# Revit family: bfs-40_210ssua2_stua2_60Hz
name_source: partatom
category: 機械設備
units: mm (PartAtom-declared; Revit-internal decimal feet)

## family parameters
OmniClass タイトル = Centrifugal Fans
OmniClass 番号 = 23.75.35.17.27
パーツ タイプ = 割り込み
ロード時にボイドで切り取り = いいえ
丸型コネクタ寸法 = 直径を使用
作業面ベース = いいえ
共有 = いいえ
常に垂直 = はい
部屋計算ポイント = はい

## types (7) — shared parameters
Clearance Left = 450  [stored 1.47638 ft]
IfcExportAs = IfcFanType
IfcExportType = CENTRIFUGALFORWARDCURVED
MID静圧 = 0.0 Pa
MID風量 = 0.0 m³/h
OmniClassCode = 23-33 31 19 13 15
URL = https://www.mitsubishielectric.co.jp
Uniclass2015Code = Pr_65_67_29_12
Uniclass2015Title = Centrifugal fans
Uniclass2015Version = Systems v1.9
サービススペース = はい
ファンの種類 = 多翼形
仕様書バージョン = Version1.0
企業コード = 108420
分類コード = 50052502100020
参照している仕様書等のバージョン = 公共建築工事標準仕様書（機械設備工事編）平成31年度版
周波数 = 60 Hz
呼称 = 消音ボックス付送風機
実風量 = 0.0 m³/h
形名 = BFS-SSUA : BFS-40SSUA
本体マテリアル = 溶融亜鉛めっき鋼板
極 = 4
法定耐用年数 = 15
盤工事区分 = 電気工事
積算_科目 = 2 換気設備
製品リリース年月 = 2022年6月1日
製品出荷対象 = 国内
製造元 = 三菱電機株式会社
設置方法 = 天吊
説明 = ストレートシロッコファン給気タイプ消音形
負荷分類 = 3_ファン類
運転質量 = 0.00 kg
zero-valued in all types: Clearance Back, Clearance Bottom, Clearance Front, Clearance Right, Clearance Top

## per-type parameters (varying)
| type | Depth | Height | M | MAX静圧 | MAX風量 | MIN静圧 | MIN風量 | Width | ダクト径 | 価格 | 天吊金具ピッチ奥行 | 天吊金具ピッチ幅 | 極数 | 消費電力 | 番手 | 相 | 製品質量 | 質量 | 電動機出力 | 電圧 | 騒音レベル(dB(A)) | 騒音レベル(dB(A))_側面 | 騒音レベル(dB(A))_吐出 | 騒音レベル(dB(A))_吸込 |
| BFS-40SSUA2 | 378  [stored 1.24016 ft] | 255  [stored 0.836614 ft] | 70  [stored 0.229659 ft] | 97.0 Pa | 400.0 m³/h | 41.0 Pa | 204.0 m³/h | 282 | 150 mm | 120000 $ | 343  [stored 1.12533 ft] | 358  [stored 1.17454 ft] | 2 | 85 W | #1 1/4 | 1 | 10.50 kg | 12.60 kg | 35 W | 100 V | 42 | 20.5 | 39 | 42 |
| BFS-50SSUA2 | 423  [stored 1.3878 ft] | 255  [stored 0.836614 ft] | 85  [stored 0.278871 ft] | 190.0 Pa | 500.0 m³/h | 120.0 Pa | 395.0 m³/h | 325  [stored 1.06627 ft] | 200 mm | 169000 $ | 388  [stored 1.27297 ft] | 401  [stored 1.31562 ft] | 2 | 100 W | #1 1/4 | 1 | 12.50 kg | 15.00 kg | 45 W | 100 V | 45.5 | 23.5 | 41 | 45.5 |
| BFS-80SSUA2 | 463  [stored 1.51903 ft] | 305  [stored 1.00066 ft] | 85  [stored 0.278871 ft] | 165.0 Pa | 800.0 m³/h | 109.0 Pa | 650.0 m³/h | 373  [stored 1.22375 ft] | 200 mm | 189000 $ | 428  [stored 1.4042 ft] | 449  [stored 1.4731 ft] | 2 | 210 W | #1 1/4 | 1 | 16.00 kg | 19.20 kg | 110 W | 100 V | 51 | 28 | 44.5 | 51 |
| BFS-100SSUA2 | 488  [stored 1.60105 ft] | 305  [stored 1.00066 ft] | 85  [stored 0.278871 ft] | 260.0 Pa | 1000.0 m³/h | 215.0 Pa | 880.0 m³/h | 393  [stored 1.28937 ft] | 200 mm | 211000 $ | 453  [stored 1.48622 ft] | 469 | 2 | 280 W | #1 1/2 | 1 | 18.00 kg | 21.60 kg | 200 W | 100 V | 53 | 32 | 51 | 53 |
| BFS-150SSUA2 | 590  [stored 1.9357 ft] | 350  [stored 1.14829 ft] | 85  [stored 0.278871 ft] | 320.0 Pa | 1500.0 m³/h | 230.0 Pa | 1275.0 m³/h | 391 | 250 mm | 243000 $ | 555  [stored 1.82087 ft] | 467  [stored 1.53215 ft] | 2 | 515 W | #1 1/2 | 1 | 23.50 kg | 28.20 kg | 300 W | 100 V | 60.5 | 35 | 56 | 60.5 |
| BFS-150STUA2 | 590  [stored 1.9357 ft] | 350  [stored 1.14829 ft] | 85  [stored 0.278871 ft] | 320.0 Pa | 1500.0 m³/h | 175.0 Pa | 1110.0 m³/h | 391 | 250 mm | 243000 $ | 555  [stored 1.82087 ft] | 467  [stored 1.53215 ft] | 3 | 440 W | #1 1/2 | 3 | 23.50 kg | 28.20 kg | 350 W | 200 V | 57.5 | 35 | 56 | 57.5 |
| BFS-210STUA2 | 645  [stored 2.11614 ft] | 350  [stored 1.14829 ft] | 100  [stored 0.328084 ft] | 325.0 Pa | 2100.0 m³/h | 0.0 Pa | 0.0 m³/h | 476  [stored 1.56168 ft] | 300 mm | 373000 $ | 610  [stored 2.00131 ft] | 552  [stored 1.81102 ft] | 3 | 700 W | #1 1/2 | 3 | 26.50 kg | 31.80 kg | 490 W | 200 V | 64.5 | 38 | 59.5 | 64.5 |

note: column(s) folded — value = type name in every type: モデル

note: [stored X ft] marks values corroborated as IEEE doubles in the binary element streams (Revit-internal decimal feet)
